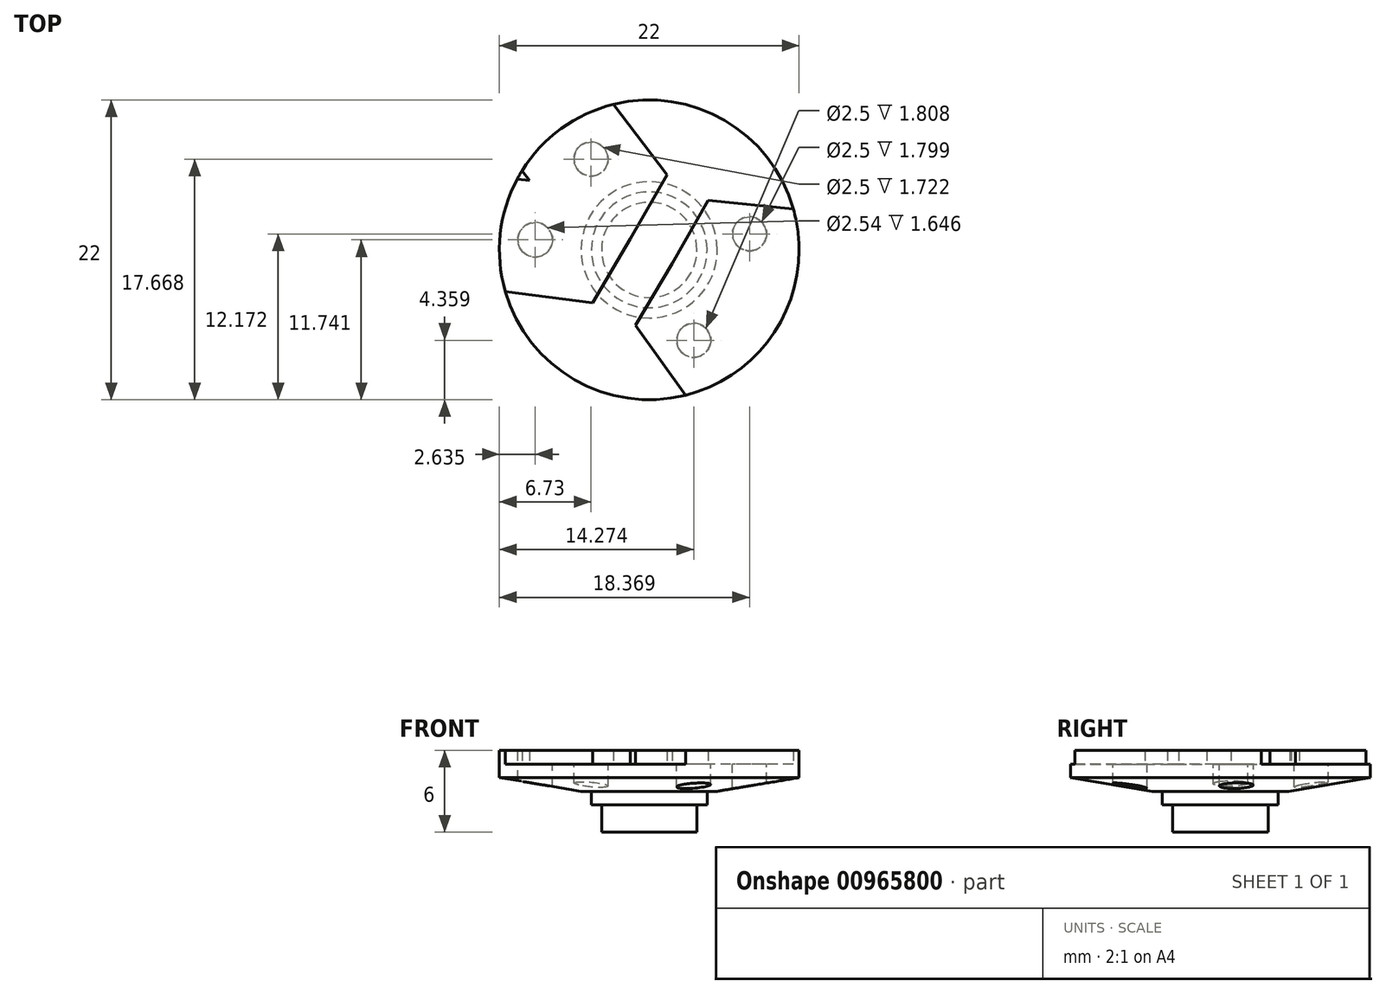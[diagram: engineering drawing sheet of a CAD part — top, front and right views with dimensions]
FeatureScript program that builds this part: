
annotation { "Feature Type Name" : "Feature", "Feature Type Description" : "" }
export const myFeature = defineFeature(function(context is Context, id is Id, definition is map)
    precondition{}
    {
        {
            var Q0;
            Q0=qCreatedBy(makeId("Top.planeOp"),FACE);
            var sketch = newSketch(context, id + "F0", { "sketchPlane" : qUnion([Q0])});
            skPoint(sketch, "E0.first.point", {"position": v(-27, 32.4) * mm});
            skPoint(sketch, "E0.second.point", {"position": v(40.45, 8.89) * mm});
            skPoint(sketch, "E0.third.point", {"position": v(-9.64, -40.66) * mm});
            skLineSegment(sketch, "E1", {"start": v(-1.8, 0.92) * mm, "end": v(-4.57, -3.75) * mm});
            skLineSegment(sketch, "E2", {"start": v(-4.57, -3.75) * mm, "end": v(-11, -2.93) * mm});
            skLineSegment(sketch, "E3", {"start": v(-10.12, 5.32) * mm, "end": v(-9.22, 5.2) * mm});
            skLineSegment(sketch, "E4", {"start": v(2.24, -10.55) * mm, "end": v(-1.42, -5.43) * mm});
            skLineSegment(sketch, "E5", {"start": v(-1.42, -5.43) * mm, "end": v(1.27, -0.86) * mm});
            skLineSegment(sketch, "E6.MirrorCS", {"start": v(10.15, 3.12) * mm, "end": v(3.89, 3.75) * mm});
            skLineSegment(sketch, "E7.MirrorCS", {"start": v(3.89, 3.75) * mm, "end": v(1.27, -0.86) * mm});
            skLineSegment(sketch, "E8.MirrorCS", {"start": v(-1.8, 0.92) * mm, "end": v(0.87, 5.64) * mm});
            skLineSegment(sketch, "E9.MirrorCS", {"start": v(0.87, 5.64) * mm, "end": v(-3.04, 10.8) * mm});
            skLineSegment(sketch, "E10.MirrorCS", {"start": v(-9.77, 5.93) * mm, "end": v(-9.22, 5.2) * mm});
            skCircle(sketch, "E11", {"center": v(-0.43, 0.12) * mm, "radius": 11 * mm});
            skCircle(sketch, "E12", {"center": v(-0.43, 0.12) * mm, "radius": 3.5 * mm});
            skCircle(sketch, "E13", {"center": v(-0.43, 0.12) * mm, "radius": 4.25 * mm});
            skPoint(sketch, "E14.end.orphan", {"position": v(-34.95, 0.12) * mm});
            skSolve(sketch);
        }
        {
            var Q0;
            {var subQ5=sQuery(id+"F0.wireOp",EDGE,"E1");Q0=makeQuery(id+"F0.imprint","IMPRINT",FACE,{"disambiguationData":[TD([[makeQuery(id+"F0.imprint","IMPRINT",EDGE,{"derivedFrom":subQ5}),1.0]])]});}
            var Q1;
            Q1=makeQuery(id+"F2.opExtrude","CAP_FACE",FACE,{"disambiguationData":[OSD([sQuery(id+"F0.wireOp",EDGE,"E1"),sQuery(id+"F0.wireOp",EDGE,"E2"),sQuery(id+"F0.wireOp",EDGE,"E3"),sQuery(id+"F0.wireOp",EDGE,"E8.MirrorCS"),sQuery(id+"F0.wireOp",EDGE,"E9.MirrorCS"),sQuery(id+"F0.wireOp",EDGE,"E10.MirrorCS"),sQuery(id+"F0.wireOp",EDGE,"E11")])],"isStart":false});
            var Q2;
            Q2=makeQuery(id+"F2.opExtrude","CAP_FACE",FACE,{"disambiguationData":[OSD([sQuery(id+"F0.wireOp",EDGE,"E4"),sQuery(id+"F0.wireOp",EDGE,"E5"),sQuery(id+"F0.wireOp",EDGE,"E6.MirrorCS"),sQuery(id+"F0.wireOp",EDGE,"E7.MirrorCS"),sQuery(id+"F0.wireOp",EDGE,"E11")])],"isStart":false});
            var Q3;
            {var subQ0=sQuery(id+"F0.wireOp",EDGE,"E10.MirrorCS");var subQ1=sQuery(id+"F0.wireOp",EDGE,"E3");var subQ2=makeQuery(id+"F0.imprint","INTERSECT",VERTEX,{"derivedFrom":[subQ1,subQ0]});Q3=makeQuery(id+"F0.imprint","IMPRINT",FACE,{"disambiguationData":[TD([[makeQuery(id+"F0.imprint","IMPRINT",EDGE,{"disambiguationData":[TD([[subQ2,1.0]])],"derivedFrom":subQ1}),1.0]])]});}
            var Q4;
            {var subQ1=sQuery(id+"F0.wireOp",EDGE,"E5");Q4=makeQuery(id+"F0.imprint","IMPRINT",FACE,{"disambiguationData":[TD([[makeQuery(id+"F0.imprint","IMPRINT",EDGE,{"derivedFrom":subQ1}),-1.0]])]});}
            var Q5;
            {var subQ7=sQuery(id+"F0.wireOp",EDGE,"E1");Q5=makeQuery(id+"F0.imprint","IMPRINT",FACE,{"disambiguationData":[TD([[makeQuery(id+"F0.imprint","IMPRINT",EDGE,{"derivedFrom":subQ7}),-1.0]])]});}
            var Q6;
            {var subQ6=sQuery(id+"F0.wireOp",EDGE,"E1");var subQ10=sQuery(id+"F0.wireOp",EDGE,"E2");var subQ11=makeQuery(id+"F0.imprint","INTERSECT",VERTEX,{"derivedFrom":[subQ6,subQ10]});Q6=makeQuery(id+"F0.imprint","IMPRINT",FACE,{"disambiguationData":[TD([[makeQuery(id+"F0.imprint","IMPRINT",EDGE,{"disambiguationData":[TD([[subQ11,1.0]])],"derivedFrom":subQ6}),-1.0]])]});}
            var Q7;
            {var subQ0=sQuery(id+"F0.wireOp",EDGE,"E12");var subQ1=sQuery(id+"F0.wireOp",EDGE,"E1");var subQ2=makeQuery(id+"F0.imprint","INTERSECT",VERTEX,{"derivedFrom":[subQ1,subQ0]});Q7=makeQuery(id+"F0.imprint","IMPRINT",FACE,{"disambiguationData":[TD([[makeQuery(id+"F0.imprint","IMPRINT",EDGE,{"disambiguationData":[TD([[subQ2,-1.0]])],"derivedFrom":subQ1}),-1.0]])]});}
            var Q8;
            {var subQ7=sQuery(id+"F0.wireOp",EDGE,"E7.MirrorCS");var subQ8=sQuery(id+"F0.wireOp",EDGE,"E6.MirrorCS");var subQ9=makeQuery(id+"F0.imprint","INTERSECT",VERTEX,{"derivedFrom":[subQ8,subQ7]});Q8=makeQuery(id+"F0.imprint","IMPRINT",FACE,{"disambiguationData":[TD([[makeQuery(id+"F0.imprint","IMPRINT",EDGE,{"disambiguationData":[TD([[subQ9,1.0]])],"derivedFrom":subQ8}),-1.0]])]});}
            var Q9;
            {var subQ0=sQuery(id+"F0.wireOp",EDGE,"E13");var subQ1=sQuery(id+"F0.wireOp",EDGE,"E7.MirrorCS");var subQ2=makeQuery(id+"F0.imprint","INTERSECT",VERTEX,{"derivedFrom":[subQ1,subQ0]});Q9=makeQuery(id+"F0.imprint","IMPRINT",FACE,{"disambiguationData":[TD([[makeQuery(id+"F0.imprint","IMPRINT",EDGE,{"disambiguationData":[TD([[subQ2,-1.0]])],"derivedFrom":subQ1}),-1.0]])]});}
            var Q10;
            {var subQ6=sQuery(id+"F0.wireOp",EDGE,"E8.MirrorCS");var subQ8=sQuery(id+"F0.wireOp",EDGE,"E1");var subQ9=makeQuery(id+"F0.imprint","INTERSECT",VERTEX,{"derivedFrom":[subQ8,subQ6]});Q10=makeQuery(id+"F0.imprint","IMPRINT",FACE,{"disambiguationData":[TD([[makeQuery(id+"F0.imprint","IMPRINT",EDGE,{"disambiguationData":[TD([[subQ9,-1.0]])],"derivedFrom":subQ8}),1.0]])]});}
            var Q11;
            {var subQ0=sQuery(id+"F0.wireOp",EDGE,"E13");var subQ1=sQuery(id+"F0.wireOp",EDGE,"E5");var subQ2=makeQuery(id+"F0.imprint","INTERSECT",VERTEX,{"derivedFrom":[subQ1,subQ0]});Q11=makeQuery(id+"F0.imprint","IMPRINT",FACE,{"disambiguationData":[TD([[makeQuery(id+"F0.imprint","IMPRINT",EDGE,{"disambiguationData":[TD([[subQ2,-1.0]])],"derivedFrom":subQ1}),-1.0]])]});}
            var Q12;
            {var subQ7=sQuery(id+"F0.wireOp",EDGE,"E5");var subQ8=sQuery(id+"F0.wireOp",EDGE,"E4");var subQ9=makeQuery(id+"F0.imprint","INTERSECT",VERTEX,{"derivedFrom":[subQ8,subQ7]});Q12=makeQuery(id+"F0.imprint","IMPRINT",FACE,{"disambiguationData":[TD([[makeQuery(id+"F0.imprint","IMPRINT",EDGE,{"disambiguationData":[TD([[subQ9,1.0]])],"derivedFrom":subQ8}),-1.0]])]});}
            var Q13;
            {var subQ6=sQuery(id+"F0.wireOp",EDGE,"E2");var subQ9=sQuery(id+"F0.wireOp",EDGE,"E1");var subQ10=makeQuery(id+"F0.imprint","INTERSECT",VERTEX,{"derivedFrom":[subQ9,subQ6]});Q13=makeQuery(id+"F0.imprint","IMPRINT",FACE,{"disambiguationData":[TD([[makeQuery(id+"F0.imprint","IMPRINT",EDGE,{"disambiguationData":[TD([[subQ10,1.0]])],"derivedFrom":subQ9}),1.0]])]});}
            extrude(context, id + "F1", {"entities" : qUnion([Q0, Q1, Q2, Q3, Q4, Q5, Q6, Q7, Q8, Q9, Q10, Q11, Q12, Q13]), "oppositeDirection" : true, "depth" : 2 * mm, "offsetDistance" : 25 * mm});
        }
        {
            var Q0;
            {var subQ7=sQuery(id+"F0.wireOp",EDGE,"E1");Q0=makeQuery(id+"F0.imprint","IMPRINT",FACE,{"disambiguationData":[TD([[makeQuery(id+"F0.imprint","IMPRINT",EDGE,{"derivedFrom":subQ7}),-1.0]])]});}
            var Q1;
            {var subQ1=sQuery(id+"F0.wireOp",EDGE,"E5");Q1=makeQuery(id+"F0.imprint","IMPRINT",FACE,{"disambiguationData":[TD([[makeQuery(id+"F0.imprint","IMPRINT",EDGE,{"derivedFrom":subQ1}),-1.0]])]});}
            var Q2;
            {var subQ0=sQuery(id+"F0.wireOp",EDGE,"E12");var subQ1=sQuery(id+"F0.wireOp",EDGE,"E1");var subQ2=makeQuery(id+"F0.imprint","INTERSECT",VERTEX,{"derivedFrom":[subQ1,subQ0]});Q2=makeQuery(id+"F0.imprint","IMPRINT",FACE,{"disambiguationData":[TD([[makeQuery(id+"F0.imprint","IMPRINT",EDGE,{"disambiguationData":[TD([[subQ2,-1.0]])],"derivedFrom":subQ1}),-1.0]])]});}
            var Q3;
            {var subQ6=sQuery(id+"F0.wireOp",EDGE,"E1");var subQ10=sQuery(id+"F0.wireOp",EDGE,"E2");var subQ11=makeQuery(id+"F0.imprint","INTERSECT",VERTEX,{"derivedFrom":[subQ6,subQ10]});Q3=makeQuery(id+"F0.imprint","IMPRINT",FACE,{"disambiguationData":[TD([[makeQuery(id+"F0.imprint","IMPRINT",EDGE,{"disambiguationData":[TD([[subQ11,1.0]])],"derivedFrom":subQ6}),-1.0]])]});}
            var Q4;
            {var subQ7=sQuery(id+"F0.wireOp",EDGE,"E5");var subQ8=sQuery(id+"F0.wireOp",EDGE,"E4");var subQ9=makeQuery(id+"F0.imprint","INTERSECT",VERTEX,{"derivedFrom":[subQ8,subQ7]});Q4=makeQuery(id+"F0.imprint","IMPRINT",FACE,{"disambiguationData":[TD([[makeQuery(id+"F0.imprint","IMPRINT",EDGE,{"disambiguationData":[TD([[subQ9,1.0]])],"derivedFrom":subQ8}),-1.0]])]});}
            var Q5;
            {var subQ0=sQuery(id+"F0.wireOp",EDGE,"E13");var subQ1=sQuery(id+"F0.wireOp",EDGE,"E5");var subQ2=makeQuery(id+"F0.imprint","INTERSECT",VERTEX,{"derivedFrom":[subQ1,subQ0]});Q5=makeQuery(id+"F0.imprint","IMPRINT",FACE,{"disambiguationData":[TD([[makeQuery(id+"F0.imprint","IMPRINT",EDGE,{"disambiguationData":[TD([[subQ2,-1.0]])],"derivedFrom":subQ1}),-1.0]])]});}
            extrude(context, id + "F2", {"entities" : qUnion([Q0, Q1, Q2, Q3, Q4, Q5]), "depth" : 1 * mm, "offsetDistance" : 25 * mm});
        }
        {
            var Q0;
            {var subQ0=sQuery(id+"F0.wireOp",EDGE,"E8.MirrorCS");var subQ1=sQuery(id+"F0.wireOp",EDGE,"E1");var subQ2=makeQuery(id+"F0.imprint","INTERSECT",VERTEX,{"derivedFrom":[subQ1,subQ0]});Q0=makeQuery(id+"F0.imprint","IMPRINT",FACE,{"disambiguationData":[TD([[makeQuery(id+"F0.imprint","IMPRINT",EDGE,{"disambiguationData":[TD([[subQ2,-1.0]])],"derivedFrom":subQ1}),-1.0]])]});}
            var Q1;
            {var subQ6=sQuery(id+"F0.wireOp",EDGE,"E8.MirrorCS");var subQ8=sQuery(id+"F0.wireOp",EDGE,"E1");var subQ9=makeQuery(id+"F0.imprint","INTERSECT",VERTEX,{"derivedFrom":[subQ8,subQ6]});Q1=makeQuery(id+"F0.imprint","IMPRINT",FACE,{"disambiguationData":[TD([[makeQuery(id+"F0.imprint","IMPRINT",EDGE,{"disambiguationData":[TD([[subQ9,-1.0]])],"derivedFrom":subQ8}),1.0]])]});}
            var Q2;
            {var subQ0=sQuery(id+"F0.wireOp",EDGE,"E7.MirrorCS");var subQ1=sQuery(id+"F0.wireOp",EDGE,"E5");var subQ2=makeQuery(id+"F0.imprint","INTERSECT",VERTEX,{"derivedFrom":[subQ1,subQ0]});Q2=makeQuery(id+"F0.imprint","IMPRINT",FACE,{"disambiguationData":[TD([[makeQuery(id+"F0.imprint","IMPRINT",EDGE,{"disambiguationData":[TD([[subQ2,1.0]])],"derivedFrom":subQ1}),-1.0]])]});}
            extrude(context, id + "F3", {"entities" : qUnion([Q0, Q1, Q2]), "oppositeDirection" : true, "depth" : 5 * mm, "offsetDistance" : 25 * mm});
        }
        {
            var Q0;
            {var subQ0=sQuery(id+"F0.wireOp",EDGE,"E13");var subQ1=sQuery(id+"F0.wireOp",EDGE,"E5");var subQ2=makeQuery(id+"F0.imprint","INTERSECT",VERTEX,{"derivedFrom":[subQ1,subQ0]});Q0=makeQuery(id+"F0.imprint","IMPRINT",FACE,{"disambiguationData":[TD([[makeQuery(id+"F0.imprint","IMPRINT",EDGE,{"disambiguationData":[TD([[subQ2,-1.0]])],"derivedFrom":subQ1}),-1.0]])]});}
            var Q1;
            {var subQ0=sQuery(id+"F0.wireOp",EDGE,"E12");var subQ1=sQuery(id+"F0.wireOp",EDGE,"E1");var subQ2=makeQuery(id+"F0.imprint","INTERSECT",VERTEX,{"derivedFrom":[subQ1,subQ0]});Q1=makeQuery(id+"F0.imprint","IMPRINT",FACE,{"disambiguationData":[TD([[makeQuery(id+"F0.imprint","IMPRINT",EDGE,{"disambiguationData":[TD([[subQ2,-1.0]])],"derivedFrom":subQ1}),1.0]])]});}
            var Q2;
            {var subQ0=sQuery(id+"F0.wireOp",EDGE,"E12");var subQ1=sQuery(id+"F0.wireOp",EDGE,"E1");var subQ2=makeQuery(id+"F0.imprint","INTERSECT",VERTEX,{"derivedFrom":[subQ1,subQ0]});Q2=makeQuery(id+"F0.imprint","IMPRINT",FACE,{"disambiguationData":[TD([[makeQuery(id+"F0.imprint","IMPRINT",EDGE,{"disambiguationData":[TD([[subQ2,-1.0]])],"derivedFrom":subQ1}),-1.0]])]});}
            var Q3;
            {var subQ0=sQuery(id+"F0.wireOp",EDGE,"E13");var subQ1=sQuery(id+"F0.wireOp",EDGE,"E7.MirrorCS");var subQ2=makeQuery(id+"F0.imprint","INTERSECT",VERTEX,{"derivedFrom":[subQ1,subQ0]});Q3=makeQuery(id+"F0.imprint","IMPRINT",FACE,{"disambiguationData":[TD([[makeQuery(id+"F0.imprint","IMPRINT",EDGE,{"disambiguationData":[TD([[subQ2,-1.0]])],"derivedFrom":subQ1}),-1.0]])]});}
            var Q4;
            {var subQ6=sQuery(id+"F0.wireOp",EDGE,"E8.MirrorCS");var subQ8=sQuery(id+"F0.wireOp",EDGE,"E1");var subQ9=makeQuery(id+"F0.imprint","INTERSECT",VERTEX,{"derivedFrom":[subQ8,subQ6]});Q4=makeQuery(id+"F0.imprint","IMPRINT",FACE,{"disambiguationData":[TD([[makeQuery(id+"F0.imprint","IMPRINT",EDGE,{"disambiguationData":[TD([[subQ9,-1.0]])],"derivedFrom":subQ8}),1.0]])]});}
            var Q5;
            {var subQ0=sQuery(id+"F0.wireOp",EDGE,"E7.MirrorCS");var subQ1=sQuery(id+"F0.wireOp",EDGE,"E5");var subQ2=makeQuery(id+"F0.imprint","INTERSECT",VERTEX,{"derivedFrom":[subQ1,subQ0]});Q5=makeQuery(id+"F0.imprint","IMPRINT",FACE,{"disambiguationData":[TD([[makeQuery(id+"F0.imprint","IMPRINT",EDGE,{"disambiguationData":[TD([[subQ2,1.0]])],"derivedFrom":subQ1}),-1.0]])]});}
            var Q6;
            {var subQ0=sQuery(id+"F0.wireOp",EDGE,"E8.MirrorCS");var subQ1=sQuery(id+"F0.wireOp",EDGE,"E1");var subQ2=makeQuery(id+"F0.imprint","INTERSECT",VERTEX,{"derivedFrom":[subQ1,subQ0]});Q6=makeQuery(id+"F0.imprint","IMPRINT",FACE,{"disambiguationData":[TD([[makeQuery(id+"F0.imprint","IMPRINT",EDGE,{"disambiguationData":[TD([[subQ2,-1.0]])],"derivedFrom":subQ1}),-1.0]])]});}
            extrude(context, id + "F4", {"entities" : qUnion([Q0, Q1, Q2, Q3, Q4, Q5, Q6]), "operationType" : NewBodyOperationType.ADD, "oppositeDirection" : true, "depth" : 3 * mm, "offsetDistance" : 25 * mm});
        }
        {
            var Q0;
            Q0=makeQuery(id+"F1.opExtrude","CAP_EDGE",EDGE,{"disambiguationData":[OSD([sQuery(id+"F0.wireOp",EDGE,"E11")])],"isStart":false});
            chamfer(context, id + "F5", {"entities" : qUnion([Q0]), "chamferType" : ChamferType.TWO_OFFSETS, "width1" : 1 * mm, "oppositeDirection" : false, "width2" : 6 * mm, "tangentPropagation" : true});
        }
        {
            var Q0;
            Q0=qCreatedBy(makeId("Top.planeOp"),FACE);
            var sketch = newSketch(context, id + "F6", { "sketchPlane" : qUnion([Q0])});
            skCircle(sketch, "E15", {"center": v(-8.8, 0.86) * mm, "radius": 1.27 * mm});
            skCircle(sketch, "E16", {"center": v(-4.7, 6.79) * mm, "radius": 1.25 * mm});
            skCircle(sketch, "E17", {"center": v(2.84, -6.52) * mm, "radius": 1.25 * mm});
            skCircle(sketch, "E18", {"center": v(6.94, 1.3) * mm, "radius": 1.25 * mm});
            skSolve(sketch);
        }
        {
            var Q0;
            Q0=makeQuery(id+"F6.imprint","IMPRINT",FACE,{"disambiguationData":[TD([[makeQuery(id+"F6.imprint","IMPRINT",EDGE,{"derivedFrom":sQuery(id+"F6.wireOp",EDGE,"E15")}),1.0]])]});
            var Q1;
            Q1=makeQuery(id+"F6.imprint","IMPRINT",FACE,{"disambiguationData":[TD([[makeQuery(id+"F6.imprint","IMPRINT",EDGE,{"derivedFrom":sQuery(id+"F6.wireOp",EDGE,"E16")}),1.0]])]});
            var Q2;
            Q2=makeQuery(id+"F6.imprint","IMPRINT",FACE,{"disambiguationData":[TD([[makeQuery(id+"F6.imprint","IMPRINT",EDGE,{"derivedFrom":sQuery(id+"F6.wireOp",EDGE,"E17")}),1.0]])]});
            var Q3;
            Q3=makeQuery(id+"F6.imprint","IMPRINT",FACE,{"disambiguationData":[TD([[makeQuery(id+"F6.imprint","IMPRINT",EDGE,{"derivedFrom":sQuery(id+"F6.wireOp",EDGE,"E18")}),1.0]])]});
            extrude(context, id + "F7", {"entities" : qUnion([Q0, Q1, Q2, Q3]), "operationType" : NewBodyOperationType.ADD, "oppositeDirection" : true, "depth" : .75 * mm, "offsetDistance" : 25 * mm});
        }
        {
            var Q0;
            Q0=makeQuery(id+"F6.imprint","IMPRINT",FACE,{"disambiguationData":[TD([[makeQuery(id+"F6.imprint","IMPRINT",EDGE,{"derivedFrom":sQuery(id+"F6.wireOp",EDGE,"E15")}),1.0]])]});
            var Q1;
            Q1=makeQuery(id+"F6.imprint","IMPRINT",FACE,{"disambiguationData":[TD([[makeQuery(id+"F6.imprint","IMPRINT",EDGE,{"derivedFrom":sQuery(id+"F6.wireOp",EDGE,"E16")}),1.0]])]});
            var Q2;
            Q2=makeQuery(id+"F6.imprint","IMPRINT",FACE,{"disambiguationData":[TD([[makeQuery(id+"F6.imprint","IMPRINT",EDGE,{"derivedFrom":sQuery(id+"F6.wireOp",EDGE,"E18")}),1.0]])]});
            var Q3;
            Q3=makeQuery(id+"F6.imprint","IMPRINT",FACE,{"disambiguationData":[TD([[makeQuery(id+"F6.imprint","IMPRINT",EDGE,{"derivedFrom":sQuery(id+"F6.wireOp",EDGE,"E17")}),1.0]])]});
            extrude(context, id + "F8", {"entities" : qUnion([Q0, Q1, Q2, Q3]), "operationType" : NewBodyOperationType.REMOVE, "oppositeDirection" : true, "depth" : 3 * mm, "offsetDistance" : 25 * mm});
        }
    });
